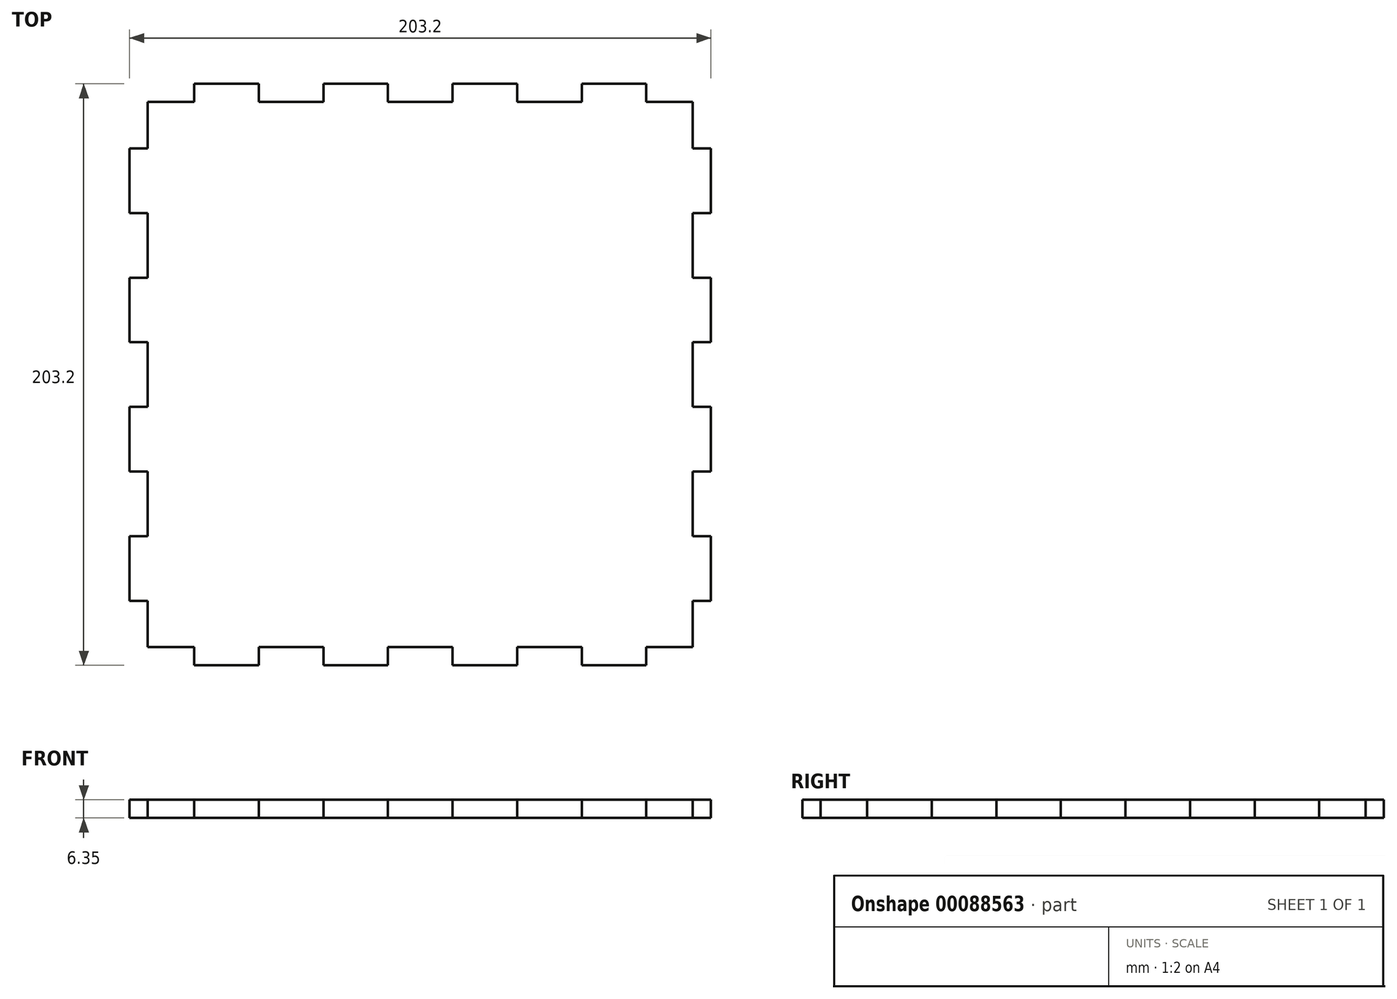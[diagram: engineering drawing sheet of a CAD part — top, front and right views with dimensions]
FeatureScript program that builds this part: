
annotation { "Feature Type Name" : "Feature", "Feature Type Description" : "" }
export const myFeature = defineFeature(function(context is Context, id is Id, definition is map)
    precondition{}
    {
        {
            var Q0;
            Q0=qCreatedBy(makeId("Top.planeOp"),FACE);
            var sketch = newSketch(context, id + "F0", { "sketchPlane" : qUnion([Q0])});
            skLineSegment(sketch, "E0.bottom", {"start": v(-101.6, 101.6) * mm, "end": v(95.25, 101.6) * mm, "construction": true});
            skLineSegment(sketch, "E0.top", {"start": v(-101.6, -101.6) * mm, "end": v(101.6, -101.6) * mm, "construction": true});
            skLineSegment(sketch, "E0.left", {"start": v(-101.6, 101.6) * mm, "end": v(-101.6, -101.6) * mm, "construction": true});
            skLineSegment(sketch, "E0.right", {"start": v(101.6, 101.6) * mm, "end": v(101.6, -101.6) * mm, "construction": true});
            skPoint(sketch, "E0.middle", {"position": v(0, 0) * mm});
            skLineSegment(sketch, "E1.bottom", {"start": v(-95.25, 95.25) * mm, "end": v(95.25, 95.25) * mm, "construction": true});
            skLineSegment(sketch, "E1.top", {"start": v(-95.25, -95.25) * mm, "end": v(95.25, -95.25) * mm, "construction": true});
            skLineSegment(sketch, "E1.left", {"start": v(-95.25, 95.25) * mm, "end": v(-95.25, -95.25) * mm, "construction": true});
            skLineSegment(sketch, "E1.right", {"start": v(95.25, 95.25) * mm, "end": v(95.25, -95.25) * mm, "construction": true});
            skLineSegment(sketch, "E2", {"start": v(-79.02, 101.6) * mm, "end": v(-79.02, 95.25) * mm});
            skLineSegment(sketch, "E3", {"start": v(-56.44, 101.6) * mm, "end": v(-56.44, 95.25) * mm});
            skLineSegment(sketch, "E4", {"start": v(-33.87, 101.6) * mm, "end": v(-33.87, 95.25) * mm});
            skLineSegment(sketch, "E5", {"start": v(-11.29, 101.6) * mm, "end": v(-11.29, 95.25) * mm});
            skLineSegment(sketch, "E6", {"start": v(11.29, 101.6) * mm, "end": v(11.29, 95.25) * mm});
            skLineSegment(sketch, "E7", {"start": v(33.87, 101.6) * mm, "end": v(33.87, 95.25) * mm});
            skLineSegment(sketch, "E8", {"start": v(56.44, 101.6) * mm, "end": v(56.44, 95.25) * mm});
            skLineSegment(sketch, "E9", {"start": v(79.02, 101.6) * mm, "end": v(79.02, 95.25) * mm});
            skLineSegment(sketch, "E10", {"start": v(95.25, 79.02) * mm, "end": v(101.6, 79.02) * mm});
            skLineSegment(sketch, "E11", {"start": v(101.6, 56.44) * mm, "end": v(95.25, 56.44) * mm});
            skLineSegment(sketch, "E12", {"start": v(95.25, 33.87) * mm, "end": v(101.6, 33.87) * mm});
            skLineSegment(sketch, "E13", {"start": v(101.6, 11.29) * mm, "end": v(95.25, 11.29) * mm});
            skLineSegment(sketch, "E14", {"start": v(-101.6, 79.02) * mm, "end": v(-95.25, 79.02) * mm});
            skLineSegment(sketch, "E15", {"start": v(-95.25, 56.44) * mm, "end": v(-101.6, 56.44) * mm});
            skLineSegment(sketch, "E16", {"start": v(-101.6, 33.87) * mm, "end": v(-95.25, 33.87) * mm});
            skLineSegment(sketch, "E17", {"start": v(-95.25, 11.29) * mm, "end": v(-101.6, 11.29) * mm});
            skLineSegment(sketch, "E18.MirrorCS", {"start": v(101.6, -11.29) * mm, "end": v(95.25, -11.29) * mm});
            skLineSegment(sketch, "E19.MirrorCS", {"start": v(101.6, -56.44) * mm, "end": v(95.25, -56.44) * mm});
            skLineSegment(sketch, "E20.MirrorCS", {"start": v(-33.87, -101.6) * mm, "end": v(-33.87, -95.25) * mm});
            skLineSegment(sketch, "E21.MirrorCS", {"start": v(11.29, -101.6) * mm, "end": v(11.29, -95.25) * mm});
            skLineSegment(sketch, "E22.MirrorCS", {"start": v(95.25, -79.02) * mm, "end": v(101.6, -79.02) * mm});
            skLineSegment(sketch, "E23.MirrorCS", {"start": v(95.25, -33.87) * mm, "end": v(101.6, -33.87) * mm});
            skLineSegment(sketch, "E24.MirrorCS", {"start": v(-11.29, -101.6) * mm, "end": v(-11.29, -95.25) * mm});
            skLineSegment(sketch, "E25.MirrorCS", {"start": v(-101.6, -33.87) * mm, "end": v(-95.25, -33.87) * mm});
            skLineSegment(sketch, "E26.MirrorCS", {"start": v(79.02, -101.6) * mm, "end": v(79.02, -95.25) * mm});
            skLineSegment(sketch, "E27.MirrorCS", {"start": v(-95.25, -56.44) * mm, "end": v(-101.6, -56.44) * mm});
            skLineSegment(sketch, "E28.MirrorCS", {"start": v(-95.25, -11.29) * mm, "end": v(-101.6, -11.29) * mm});
            skLineSegment(sketch, "E29.MirrorCS", {"start": v(-101.6, -101.6) * mm, "end": v(95.25, -101.6) * mm, "construction": true});
            skLineSegment(sketch, "E30.MirrorCS", {"start": v(-56.44, -101.6) * mm, "end": v(-56.44, -95.25) * mm});
            skLineSegment(sketch, "E31.MirrorCS", {"start": v(-101.6, -79.02) * mm, "end": v(-95.25, -79.02) * mm});
            skLineSegment(sketch, "E32.MirrorCS", {"start": v(33.87, -101.6) * mm, "end": v(33.87, -95.25) * mm});
            skLineSegment(sketch, "E33.MirrorCS", {"start": v(-95.25, -95.25) * mm, "end": v(79.02, -95.25) * mm, "construction": true});
            skLineSegment(sketch, "E34.MirrorCS", {"start": v(-79.02, -101.6) * mm, "end": v(-79.02, -95.25) * mm});
            skLineSegment(sketch, "E35.MirrorCS", {"start": v(56.44, -101.6) * mm, "end": v(56.44, -95.25) * mm});
            skPoint(sketch, "E36.end.orphan", {"position": v(-101.6, 0) * mm});
            skPoint(sketch, "E37.orphan", {"position": v(101.6, -101.6) * mm});
            skPoint(sketch, "E38.MirrorCS.start.orphan", {"position": v(95.25, -95.25) * mm});
            skPoint(sketch, "E39.MirrorCS.end.orphan", {"position": v(95.25, 0) * mm});
            skPoint(sketch, "E40.end.orphan", {"position": v(95.25, 101.6) * mm});
            skLineSegment(sketch, "E41", {"start": v(-95.25, 79.02) * mm, "end": v(-95.25, 95.25) * mm});
            skLineSegment(sketch, "E42", {"start": v(-79.02, 95.25) * mm, "end": v(-95.25, 95.25) * mm});
            skLineSegment(sketch, "E43", {"start": v(-79.02, 101.6) * mm, "end": v(-56.44, 101.6) * mm});
            skLineSegment(sketch, "E44", {"start": v(-56.44, 95.25) * mm, "end": v(-33.87, 95.25) * mm});
            skLineSegment(sketch, "E45", {"start": v(-33.87, 101.6) * mm, "end": v(-11.29, 101.6) * mm});
            skLineSegment(sketch, "E46", {"start": v(-11.29, 95.25) * mm, "end": v(11.29, 95.25) * mm});
            skLineSegment(sketch, "E47", {"start": v(11.29, 101.6) * mm, "end": v(33.87, 101.6) * mm});
            skLineSegment(sketch, "E48", {"start": v(33.87, 95.25) * mm, "end": v(56.44, 95.25) * mm});
            skLineSegment(sketch, "E49", {"start": v(56.44, 101.6) * mm, "end": v(79.02, 101.6) * mm});
            skLineSegment(sketch, "E50", {"start": v(79.02, 95.25) * mm, "end": v(95.25, 95.25) * mm});
            skLineSegment(sketch, "E51", {"start": v(95.25, 95.25) * mm, "end": v(95.25, 79.02) * mm});
            skLineSegment(sketch, "E52", {"start": v(101.6, 79.02) * mm, "end": v(101.6, 56.44) * mm});
            skLineSegment(sketch, "E53", {"start": v(95.25, 56.44) * mm, "end": v(95.25, 33.87) * mm});
            skLineSegment(sketch, "E54", {"start": v(101.6, 33.87) * mm, "end": v(101.6, 11.29) * mm});
            skLineSegment(sketch, "E55", {"start": v(95.25, 11.29) * mm, "end": v(95.25, -11.29) * mm});
            skLineSegment(sketch, "E56", {"start": v(101.6, -11.29) * mm, "end": v(101.6, -33.87) * mm});
            skLineSegment(sketch, "E57", {"start": v(95.25, -33.87) * mm, "end": v(95.25, -56.44) * mm});
            skLineSegment(sketch, "E58", {"start": v(101.6, -56.44) * mm, "end": v(101.6, -79.02) * mm});
            skLineSegment(sketch, "E59", {"start": v(95.25, -79.02) * mm, "end": v(95.25, -95.25) * mm});
            skLineSegment(sketch, "E60", {"start": v(95.25, -95.25) * mm, "end": v(79.02, -95.25) * mm});
            skLineSegment(sketch, "E61", {"start": v(79.02, -101.6) * mm, "end": v(56.44, -101.6) * mm});
            skLineSegment(sketch, "E62", {"start": v(56.44, -95.25) * mm, "end": v(33.87, -95.25) * mm});
            skLineSegment(sketch, "E63", {"start": v(33.87, -101.6) * mm, "end": v(11.29, -101.6) * mm});
            skLineSegment(sketch, "E64", {"start": v(11.29, -95.25) * mm, "end": v(-11.29, -95.25) * mm});
            skLineSegment(sketch, "E65", {"start": v(-11.29, -101.6) * mm, "end": v(-33.87, -101.6) * mm});
            skLineSegment(sketch, "E66", {"start": v(-33.87, -95.25) * mm, "end": v(-56.44, -95.25) * mm});
            skLineSegment(sketch, "E67", {"start": v(-56.44, -101.6) * mm, "end": v(-79.02, -101.6) * mm});
            skLineSegment(sketch, "E68", {"start": v(-79.02, -95.25) * mm, "end": v(-95.25, -95.25) * mm});
            skLineSegment(sketch, "E69", {"start": v(-95.25, -95.25) * mm, "end": v(-95.25, -79.02) * mm});
            skLineSegment(sketch, "E70", {"start": v(-101.6, -79.02) * mm, "end": v(-101.6, -56.44) * mm});
            skLineSegment(sketch, "E71", {"start": v(-95.25, -56.44) * mm, "end": v(-95.25, -33.87) * mm});
            skLineSegment(sketch, "E72", {"start": v(-101.6, -33.87) * mm, "end": v(-101.6, -11.29) * mm});
            skLineSegment(sketch, "E73", {"start": v(-95.25, -11.29) * mm, "end": v(-95.25, 11.29) * mm});
            skLineSegment(sketch, "E74", {"start": v(-101.6, 11.29) * mm, "end": v(-101.6, 33.87) * mm});
            skLineSegment(sketch, "E75", {"start": v(-95.25, 33.87) * mm, "end": v(-95.25, 56.44) * mm});
            skLineSegment(sketch, "E76", {"start": v(-101.6, 56.44) * mm, "end": v(-101.6, 79.02) * mm});
            skLineSegment(sketch, "E77", {"start": v(-79.02, 98.43) * mm, "end": v(-101.6, 98.43) * mm, "construction": true});
            skPoint(sketch, "E78", {"position": v(0, 95.25) * mm});
            skPoint(sketch, "E79", {"position": v(0, -95.25) * mm});
            skSolve(sketch);
        }
        {
            var Q0;
            Q0=makeQuery(id+"F0.imprint","IMPRINT",FACE,{"disambiguationData":[TD([[makeQuery(id+"F0.imprint","IMPRINT",EDGE,{"derivedFrom":sQuery(id+"F0.wireOp",EDGE,"E2")}),-1.0]])]});
            var Q1;
            Q1=makeQuery(id+"F0.imprint","IMPRINT",FACE,{"disambiguationData":[TD([[makeQuery(id+"F0.imprint","IMPRINT",EDGE,{"derivedFrom":sQuery(id+"F0.wireOp",EDGE,"E2")}),1.0]])]});
            extrude(context, id + "F1", {"entities" : qUnion([Q0, Q1]), "depth" : 6.35 * mm});
        }
    });
